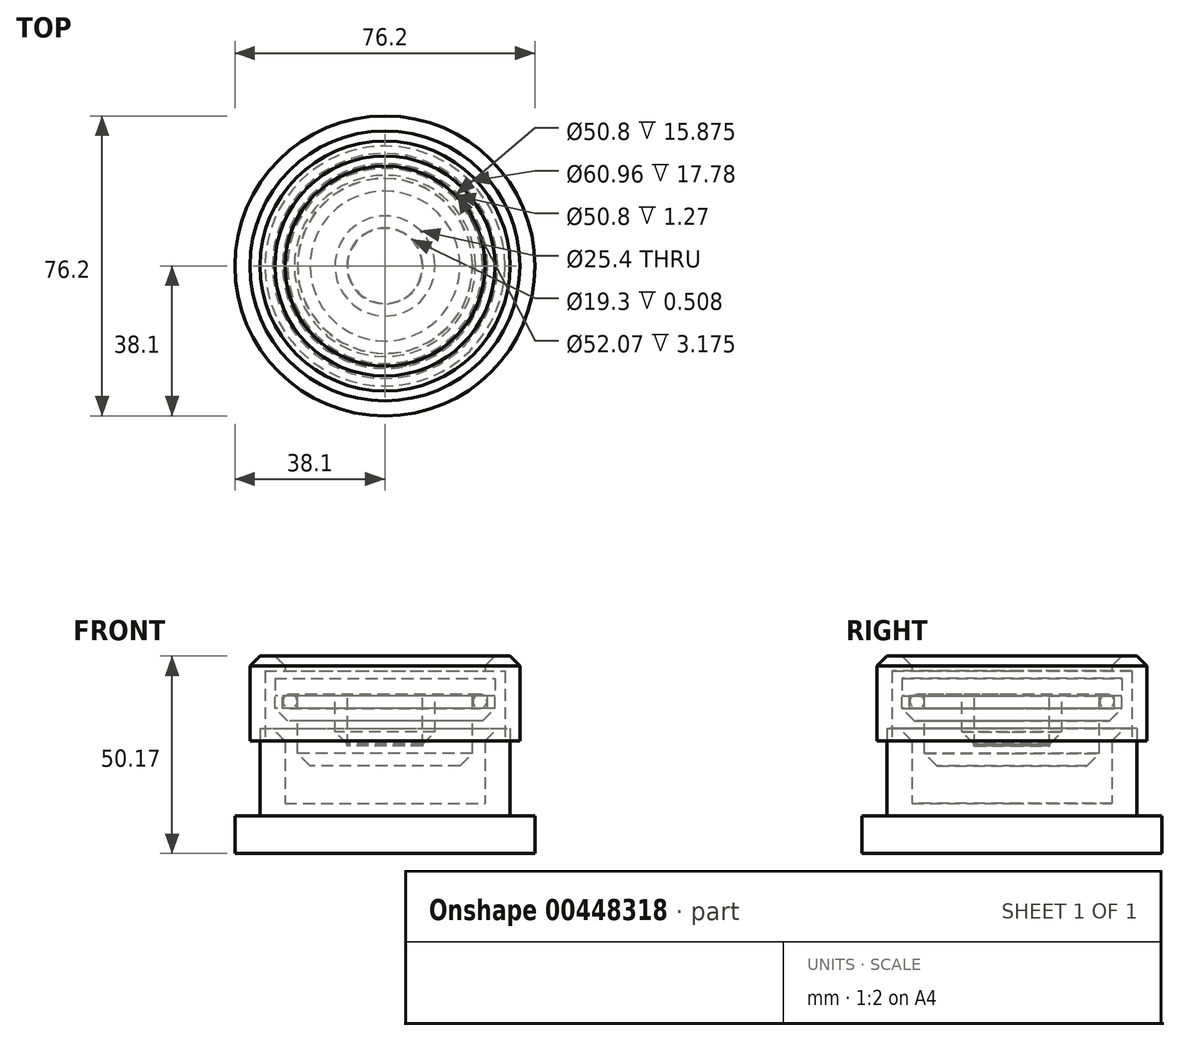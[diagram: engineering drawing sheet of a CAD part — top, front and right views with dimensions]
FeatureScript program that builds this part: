
annotation { "Feature Type Name" : "Feature", "Feature Type Description" : "" }
export const myFeature = defineFeature(function(context is Context, id is Id, definition is map)
    precondition{}
    {
        {
            var Q0;
            Q0=qCreatedBy(makeId("Front.planeOp"),FACE);
            var sketch = newSketch(context, id + "F0", { "sketchPlane" : qUnion([Q0])});
            skLineSegment(sketch, "E0", {"start": v(28.57, 22.22) * mm, "end": v(31.75, 22.22) * mm});
            skLineSegment(sketch, "E1", {"start": v(31.75, 22.22) * mm, "end": v(31.75, 0) * mm});
            skLineSegment(sketch, "E2", {"start": v(31.75, 0) * mm, "end": v(38.1, 0) * mm});
            skLineSegment(sketch, "E3", {"start": v(38.1, 0) * mm, "end": v(38.1, -9.53) * mm});
            skLineSegment(sketch, "E4", {"start": v(38.1, -9.53) * mm, "end": v(11.32, -9.53) * mm});
            skLineSegment(sketch, "E5", {"start": v(0, -9.53) * mm, "end": v(0, 3.17) * mm});
            skLineSegment(sketch, "E6", {"start": v(0, 3.17) * mm, "end": v(25.4, 3.18) * mm});
            skLineSegment(sketch, "E7", {"start": v(25.4, 3.18) * mm, "end": v(25.4, 19.05) * mm});
            skLineSegment(sketch, "E8", {"start": v(25.4, 36.83) * mm, "end": v(30.48, 36.83) * mm});
            skLineSegment(sketch, "E9", {"start": v(30.48, 36.83) * mm, "end": v(30.48, 19.05) * mm});
            skLineSegment(sketch, "E10", {"start": v(30.48, 19.05) * mm, "end": v(34.29, 19.05) * mm});
            skLineSegment(sketch, "E11", {"start": v(34.29, 19.05) * mm, "end": v(34.29, 38.1) * mm});
            skLineSegment(sketch, "E12", {"start": v(34.29, 38.1) * mm, "end": v(31.75, 40.64) * mm});
            skLineSegment(sketch, "E13", {"start": v(31.75, 40.64) * mm, "end": v(27.94, 40.64) * mm});
            skLineSegment(sketch, "E14", {"start": v(27.94, 40.64) * mm, "end": v(25.4, 38.1) * mm});
            skLineSegment(sketch, "E15", {"start": v(25.4, 38.1) * mm, "end": v(25.4, 36.83) * mm});
            skLineSegment(sketch, "E16", {"start": v(0, 17.78) * mm, "end": v(9.53, 17.78) * mm});
            skLineSegment(sketch, "E17", {"start": v(9.53, 17.78) * mm, "end": v(9.53, 30.48) * mm});
            skLineSegment(sketch, "E18", {"start": v(9.53, 30.48) * mm, "end": v(0, 30.48) * mm});
            skLineSegment(sketch, "E19", {"start": v(0, 30.48) * mm, "end": v(0, 17.78) * mm});
            skLineSegment(sketch, "E20", {"start": v(0, 17.78) * mm, "end": v(9.65, 17.78) * mm});
            skLineSegment(sketch, "E21", {"start": v(12.7, 21.34) * mm, "end": v(12.7, 30.48) * mm});
            skLineSegment(sketch, "E22", {"start": v(12.7, 30.48) * mm, "end": v(22.22, 30.48) * mm});
            skLineSegment(sketch, "E23", {"start": v(22.22, 30.48) * mm, "end": v(22.23, 27.3) * mm});
            skLineSegment(sketch, "E24", {"start": v(19.05, 12.7) * mm, "end": v(0, 12.7) * mm});
            skLineSegment(sketch, "E25", {"start": v(0, 12.7) * mm, "end": v(0, 17.78) * mm});
            skLineSegment(sketch, "E26", {"start": v(22.23, 24.13) * mm, "end": v(24.77, 24.13) * mm});
            skLineSegment(sketch, "E27", {"start": v(27.94, 27.3) * mm, "end": v(27.94, 30.48) * mm});
            skLineSegment(sketch, "E28", {"start": v(27.94, 30.48) * mm, "end": v(26.04, 30.48) * mm});
            skLineSegment(sketch, "E29", {"start": v(26.04, 30.48) * mm, "end": v(26.04, 27.3) * mm});
            skLineSegment(sketch, "E30", {"start": v(26.04, 27.3) * mm, "end": v(22.22, 27.3) * mm});
            skLineSegment(sketch, "E31.trimOffspring", {"start": v(22.23, 24.13) * mm, "end": v(22.23, 15.88) * mm});
            skCircle(sketch, "E32", {"center": v(24.13, 29.08) * mm, "radius": 1.78 * mm});
            skPoint(sketch, "E32.first.point", {"position": v(24.13, 27.3) * mm});
            skPoint(sketch, "E32.second.point", {"position": v(24.13, 30.86) * mm});
            skPoint(sketch, "E32.second.point.positionSnap0", {"position": v(24.13, 27.3) * mm});
            skPoint(sketch, "E32.third.point", {"position": v(25.87, 28.73) * mm});
            skLineSegment(sketch, "E33.bottom", {"start": v(27.94, 30.48) * mm, "end": v(0, 30.48) * mm});
            skLineSegment(sketch, "E33.top", {"start": v(27.94, 34.93) * mm, "end": v(0, 34.93) * mm});
            skLineSegment(sketch, "E33.left", {"start": v(27.94, 30.48) * mm, "end": v(27.94, 34.93) * mm});
            skLineSegment(sketch, "E33.right", {"start": v(0, 30.48) * mm, "end": v(0, 34.93) * mm});
            skLineSegment(sketch, "E34", {"start": v(22.23, 15.88) * mm, "end": v(19.05, 12.7) * mm});
            skLineSegment(sketch, "E35", {"start": v(24.77, 24.13) * mm, "end": v(27.94, 27.3) * mm});
            skLineSegment(sketch, "E36", {"start": v(11.32, -9.53) * mm, "end": v(0, -9.53) * mm});
            skPoint(sketch, "E37.orphan", {"position": v(0, -13.53) * mm});
            skLineSegment(sketch, "E38", {"start": v(9.65, 17.78) * mm, "end": v(9.65, 18.29) * mm});
            skLineSegment(sketch, "E39", {"start": v(9.65, 18.29) * mm, "end": v(12.7, 21.34) * mm});
            skLineSegment(sketch, "E40", {"start": v(28.57, 22.22) * mm, "end": v(25.4, 19.05) * mm});
            skPoint(sketch, "E41.orphan", {"position": v(25.4, 22.22) * mm});
            skSolve(sketch);
        }
        {
            var Q0;
            {var subQ0=sQuery(id+"F0.wireOp",EDGE,"E17");Q0=makeQuery(id+"F0.imprint","IMPRINT",FACE,{"disambiguationData":[TD([[makeQuery(id+"F0.imprint","IMPRINT",EDGE,{"derivedFrom":subQ0}),1.0]])]});}
            var Q1;
            Q1=sQuery(id+"F0.wireOp",EDGE,"E19");
            revolve(context, id + "F1", {"entities" : qUnion([Q0]), "axis" : qUnion([Q1]), "revolveType" : RevolveType.FULL});
        }
        {
            var Q0;
            {var subQ7=sQuery(id+"F0.wireOp",EDGE,"E21");Q0=makeQuery(id+"F0.imprint","IMPRINT",FACE,{"disambiguationData":[TD([[makeQuery(id+"F0.imprint","IMPRINT",EDGE,{"derivedFrom":subQ7}),-1.0]])]});}
            var Q1;
            Q1=sQuery(id+"F0.wireOp",EDGE,"E19");
            revolve(context, id + "F2", {"entities" : qUnion([Q0]), "axis" : qUnion([Q1]), "revolveType" : RevolveType.FULL});
        }
        {
            var Q0;
            {var subQ0=sQuery(id+"F0.wireOp",EDGE,"E33.left");Q0=makeQuery(id+"F0.imprint","IMPRINT",FACE,{"disambiguationData":[TD([[makeQuery(id+"F0.imprint","IMPRINT",EDGE,{"derivedFrom":subQ0}),1.0]])]});}
            var Q1;
            Q1=sQuery(id+"F0.wireOp",EDGE,"E33.right");
            revolve(context, id + "F3", {"entities" : qUnion([Q0]), "axis" : qUnion([Q1]), "revolveType" : RevolveType.FULL});
        }
        {
            var Q0;
            {var subQ8=sQuery(id+"F0.wireOp",EDGE,"E2");Q0=makeQuery(id+"F0.imprint","IMPRINT",FACE,{"disambiguationData":[TD([[makeQuery(id+"F0.imprint","IMPRINT",EDGE,{"derivedFrom":subQ8}),-1.0]])]});}
            var Q1;
            {var subQ0=sQuery(id+"F0.wireOp",EDGE,"E1");var subQ1=sQuery(id+"F0.wireOp",EDGE,"E0");var subQ2=makeQuery(id+"F0.imprint","INTERSECT",VERTEX,{"derivedFrom":[subQ1,subQ0]});Q1=makeQuery(id+"F0.imprint","IMPRINT",FACE,{"disambiguationData":[TD([[makeQuery(id+"F0.imprint","IMPRINT",EDGE,{"disambiguationData":[TD([[subQ2,1.0]])],"derivedFrom":subQ1}),-1.0]])]});}
            var Q2;
            Q2=sQuery(id+"F0.wireOp",EDGE,"E5");
            revolve(context, id + "F4", {"entities" : qUnion([Q0, Q1]), "axis" : qUnion([Q2]), "revolveType" : RevolveType.FULL});
        }
        {
            var Q0;
            {var subQ9=sQuery(id+"F0.wireOp",EDGE,"E8");Q0=makeQuery(id+"F0.imprint","IMPRINT",FACE,{"disambiguationData":[TD([[makeQuery(id+"F0.imprint","IMPRINT",EDGE,{"derivedFrom":subQ9}),1.0]])]});}
            var Q1;
            {var subQ0=sQuery(id+"F0.wireOp",EDGE,"E1");var subQ1=sQuery(id+"F0.wireOp",EDGE,"E0");var subQ2=makeQuery(id+"F0.imprint","INTERSECT",VERTEX,{"derivedFrom":[subQ1,subQ0]});Q1=makeQuery(id+"F0.imprint","IMPRINT",FACE,{"disambiguationData":[TD([[makeQuery(id+"F0.imprint","IMPRINT",EDGE,{"disambiguationData":[TD([[subQ2,1.0]])],"derivedFrom":subQ1}),-1.0]])]});}
            var Q2;
            Q2=sQuery(id+"F0.wireOp",EDGE,"E33.right");
            revolve(context, id + "F5", {"entities" : qUnion([Q0, Q1]), "axis" : qUnion([Q2]), "revolveType" : RevolveType.FULL});
        }
        {
            var Q0;
            {var subQ0=sQuery(id+"F0.wireOp",EDGE,"E33.bottom");var subQ1=sQuery(id+"F0.wireOp",EDGE,"E32");var subQ2=makeQuery(id+"F0.imprint","INTERSECT",VERTEX,{"disambiguationData":[OD(0.0)],"derivedFrom":[subQ1,subQ0]});Q0=makeQuery(id+"F0.imprint","IMPRINT",FACE,{"disambiguationData":[TD([[makeQuery(id+"F0.imprint","IMPRINT",EDGE,{"disambiguationData":[TD([[subQ2,1.0]])],"derivedFrom":subQ1}),1.0]])]});}
            var Q1;
            {var subQ0=sQuery(id+"F0.wireOp",EDGE,"E32");var subQ1=makeQuery(id+"F0.imprint","INTERSECT",VERTEX,{"derivedFrom":[sQuery(id+"F0.wireOp",EDGE,"E30"),subQ0]});Q1=makeQuery(id+"F0.imprint","IMPRINT",FACE,{"disambiguationData":[TD([[makeQuery(id+"F0.imprint","IMPRINT",EDGE,{"disambiguationData":[TD([[subQ1,1.0]])],"derivedFrom":subQ0}),1.0]])]});}
            var Q2;
            Q2=sQuery(id+"F0.wireOp",EDGE,"E19");
            revolve(context, id + "F6", {"entities" : qUnion([Q0, Q1]), "axis" : qUnion([Q2]), "revolveType" : RevolveType.FULL});
        }
    });
